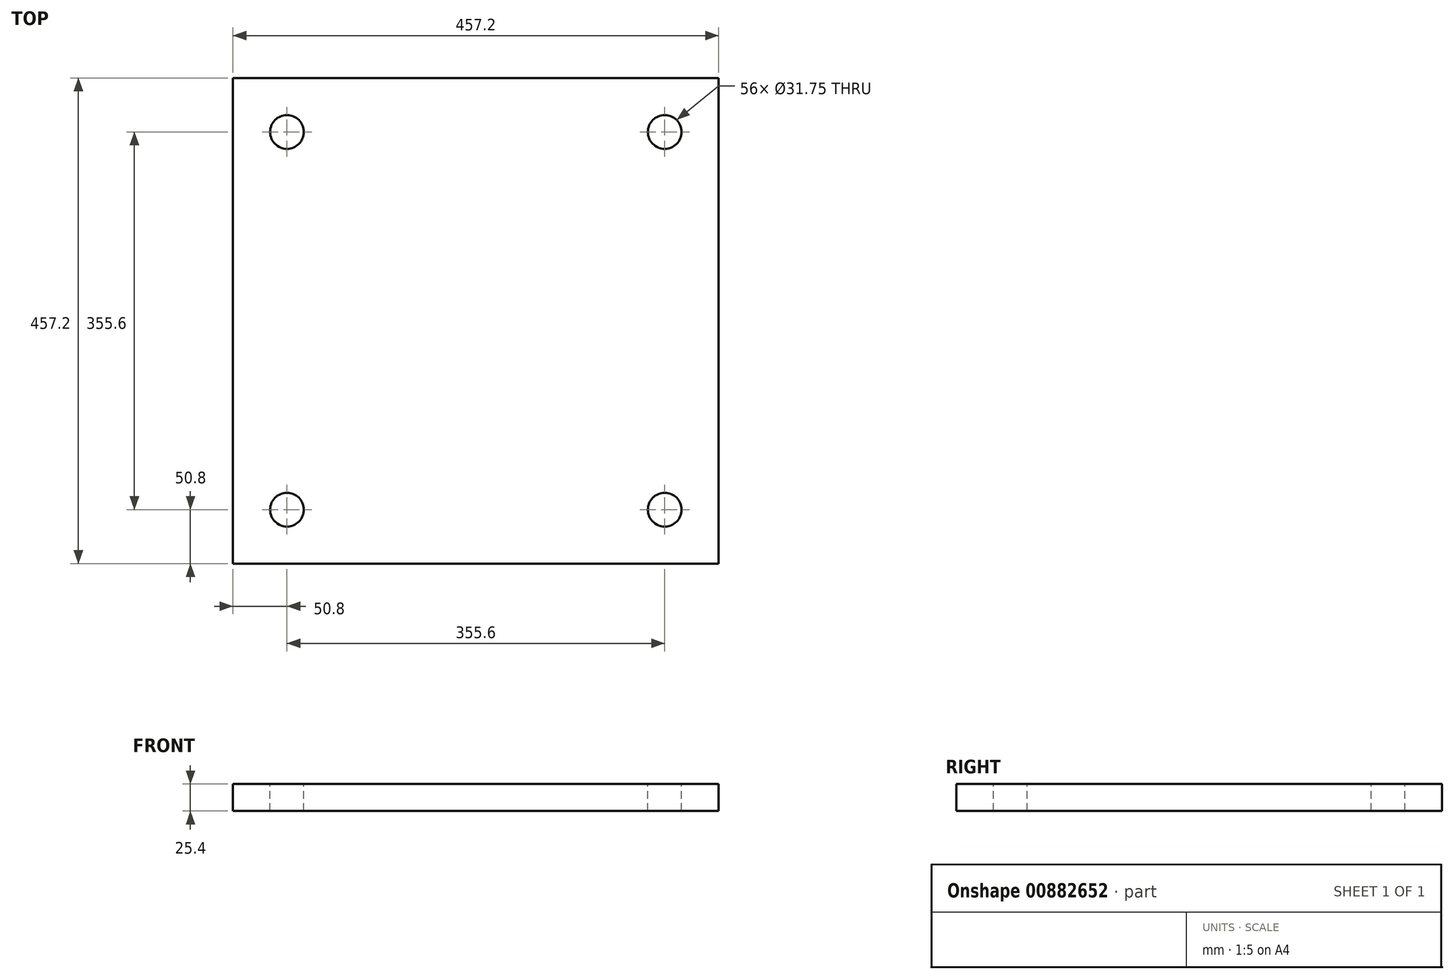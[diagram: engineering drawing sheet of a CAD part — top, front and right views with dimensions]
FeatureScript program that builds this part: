
annotation { "Feature Type Name" : "Feature", "Feature Type Description" : "" }
export const myFeature = defineFeature(function(context is Context, id is Id, definition is map)
    precondition{}
    {
        {
            var Q0;
            Q0=qCreatedBy(makeId("Top.planeOp"),FACE);
            var sketch = newSketch(context, id + "F0", { "sketchPlane" : qUnion([Q0])});
            skLineSegment(sketch, "E0.bottom", {"start": v(-228.6, 228.6) * mm, "end": v(228.6, 228.6) * mm});
            skLineSegment(sketch, "E0.top", {"start": v(-228.6, -228.6) * mm, "end": v(228.6, -228.6) * mm});
            skLineSegment(sketch, "E0.left", {"start": v(-228.6, 228.6) * mm, "end": v(-228.6, -228.6) * mm});
            skLineSegment(sketch, "E0.right", {"start": v(228.6, 228.6) * mm, "end": v(228.6, -228.6) * mm});
            skSolve(sketch);
        }
        {
            var Q0;
            Q0 = qSketchRegion(id + "F0", true);
            extrude(context, id + "F1", {"entities" : qUnion([Q0]), "depth" : 25.4 * mm, "offsetDistance" : 25.4 * mm});
        }
        {
            var Q0;
            Q0=makeQuery(id+"F1.opExtrude","CAP_FACE",FACE,{"disambiguationData":[OSD([sQuery(id+"F0.wireOp",EDGE,"E0.bottom"),sQuery(id+"F0.wireOp",EDGE,"E0.top"),sQuery(id+"F0.wireOp",EDGE,"E0.left"),sQuery(id+"F0.wireOp",EDGE,"E0.right")])],"isStart":false});
            var sketch = newSketch(context, id + "F2", { "sketchPlane" : qUnion([Q0])});
            skCircle(sketch, "E1", {"center": v(-177.8, 177.8) * mm, "radius": 15.88 * mm});
            skCircle(sketch, "E2.1.0.0", {"center": v(177.8, 177.8) * mm, "radius": 15.88 * mm});
            skLineSegment(sketch, "E2.direction1", {"start": v(-177.8, 177.8) * mm, "end": v(177.8, 177.8) * mm, "construction": true});
            skCircle(sketch, "E3.0.1.0", {"center": v(-177.8, -177.8) * mm, "radius": 15.88 * mm});
            skCircle(sketch, "E3.1.1.0", {"center": v(177.8, -177.8) * mm, "radius": 15.88 * mm});
            skLineSegment(sketch, "E3.direction2", {"start": v(-177.8, 177.8) * mm, "end": v(-177.8, -177.8) * mm, "construction": true});
            skSolve(sketch);
        }
        {
            var Q0;
            Q0=sQuery(id+"F2.wireOp",VERTEX,"E3.direction2.end");
            var Q1;
            Q1=sQuery(id+"F2.wireOp",VERTEX,"E2.direction1.start");
            var Q2;
            Q2=sQuery(id+"F2.wireOp",VERTEX,"E2.direction1.end");
            var Q3;
            Q3=sQuery(id+"F2.wireOp",VERTEX,"E3.1.1.0.center");
            var Q4;
            Q4=makeQuery(id+"F1.opExtrude","SWEPT_BODY",BODY,{"disambiguationData":[OSD([sQuery(id+"F0.wireOp",EDGE,"E0.bottom"),sQuery(id+"F0.wireOp",EDGE,"E0.top"),sQuery(id+"F0.wireOp",EDGE,"E0.left"),sQuery(id+"F0.wireOp",EDGE,"E0.right")])]});
            hole(context, id + "F3", {"style" : HoleStyle.SIMPLE, "endStyle" : HoleEndStyle.THROUGH, "holeDiameter" : 31.75 * mm, "majorDiameter" : 6.35 * mm, "isTappedThrough" : true, "tappedDepth" : 12.7 * mm, "tapClearance" : 3, "locations" : qUnion([Q0, Q1, Q2, Q3]), "scope" : qUnion([Q4])});
        }
    });
